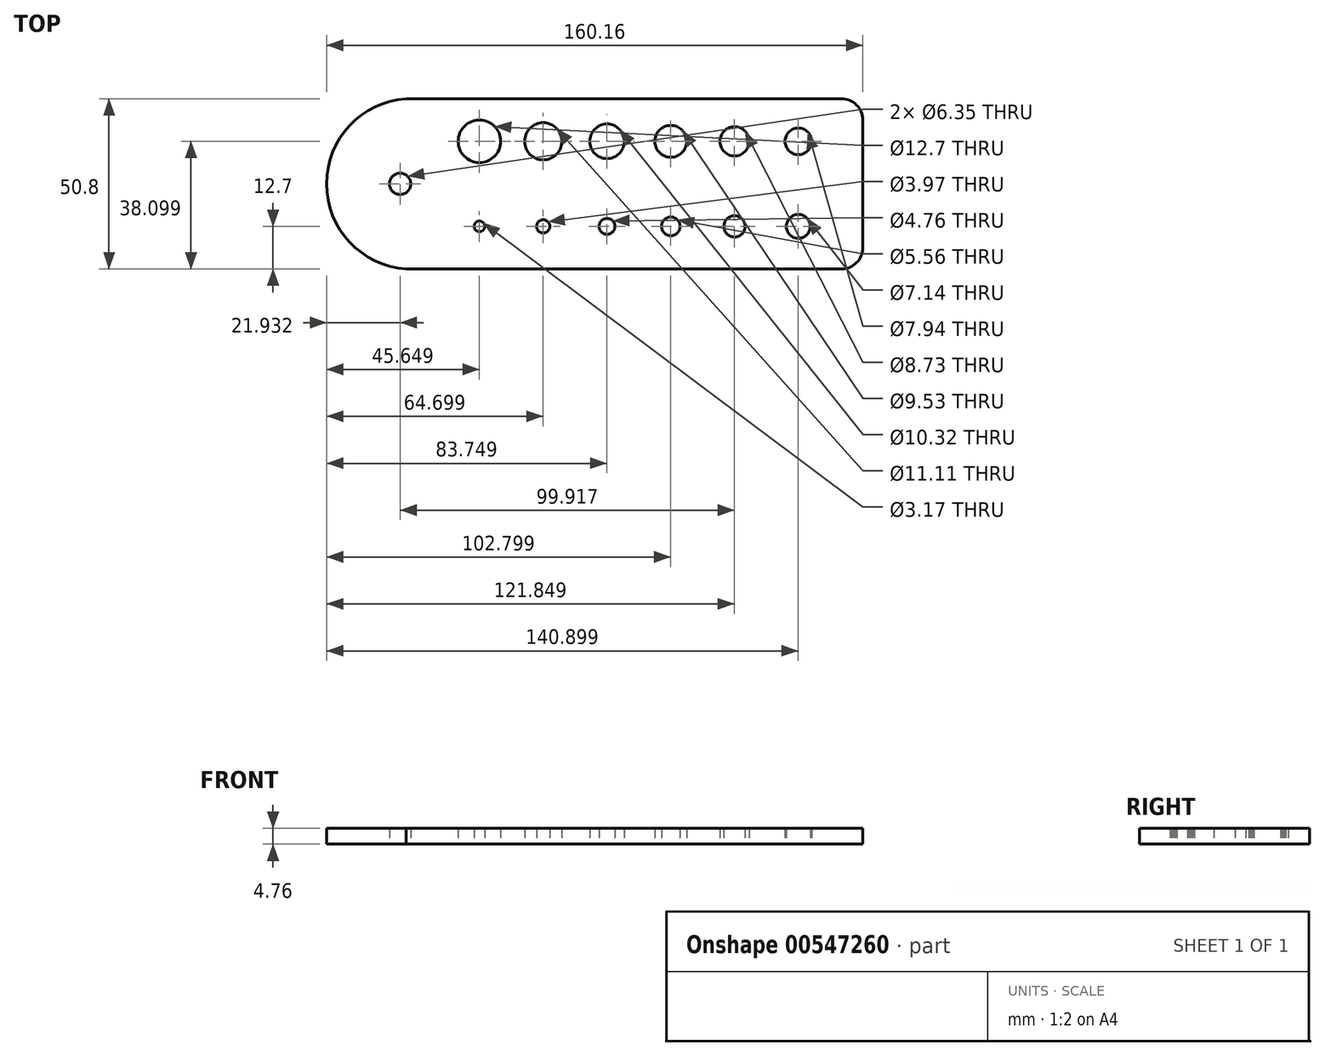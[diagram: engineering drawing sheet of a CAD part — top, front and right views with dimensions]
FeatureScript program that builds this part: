
annotation { "Feature Type Name" : "Feature", "Feature Type Description" : "" }
export const myFeature = defineFeature(function(context is Context, id is Id, definition is map)
    precondition{}
    {
        {
            var Q0;
            Q0=qCreatedBy(makeId("Top.planeOp"),FACE);
            var sketch = newSketch(context, id + "F0", { "sketchPlane" : qUnion([Q0])});
            skLineSegment(sketch, "E0.bottom", {"start": v(-46.8, 40.45) * mm, "end": v(83.22, 40.45) * mm});
            skLineSegment(sketch, "E0.top", {"start": v(-46.8, -10.35) * mm, "end": v(83.22, -10.35) * mm});
            skLineSegment(sketch, "E0.left", {"start": v(-62.83, 33.35) * mm, "end": v(-62.83, 33.35) * mm});
            skLineSegment(sketch, "E0.right", {"start": v(89.57, 34.1) * mm, "end": v(89.57, -4) * mm});
            skArc(sketch, "E1", {"start": v(-46.8, 40.45) * mm, "mid": v(-70.59, 15.05) * mm, "end": v(-46.8, -10.35) * mm});
            skPoint(sketch, "E2.visualSharp", {"position": v(89.57, -10.35) * mm});
            skArc(sketch, "E2.filletArc", {"start": v(83.22, -10.35) * mm, "mid": v(87.71, -8.5) * mm, "end": v(89.57, -4) * mm});
            skPoint(sketch, "E3.visualSharp", {"position": v(89.57, 40.45) * mm});
            skArc(sketch, "E3.filletArc", {"start": v(89.57, 34.1) * mm, "mid": v(87.71, 38.59) * mm, "end": v(83.22, 40.45) * mm});
            skSolve(sketch);
        }
        {
            var Q0;
            {var subQ5=sQuery(id+"F0.wireOp",EDGE,"E0.bottom");Q0=makeQuery(id+"F0.imprint","IMPRINT",FACE,{"disambiguationData":[TD([[makeQuery(id+"F0.imprint","IMPRINT",EDGE,{"derivedFrom":subQ5}),-1.0]])]});}
            var sketch = newSketch(context, id + "F1", { "sketchPlane" : qUnion([Q0])});
            skCircle(sketch, "E4", {"center": v(-24.94, 27.75) * mm, "radius": 6.35 * mm});
            skCircle(sketch, "E5", {"center": v(-5.9, 27.75) * mm, "radius": 5.56 * mm});
            skCircle(sketch, "E6", {"center": v(32.2, 27.75) * mm, "radius": 4.76 * mm});
            skCircle(sketch, "E7", {"center": v(51.26, 27.75) * mm, "radius": 4.37 * mm});
            skCircle(sketch, "E8", {"center": v(70.3, 27.75) * mm, "radius": 3.97 * mm});
            skCircle(sketch, "E9", {"center": v(13.16, 27.75) * mm, "radius": 5.16 * mm});
            skCircle(sketch, "E10", {"center": v(51.26, 2.35) * mm, "radius": 3.18 * mm});
            skCircle(sketch, "E11", {"center": v(32.2, 2.35) * mm, "radius": 2.78 * mm});
            skCircle(sketch, "E12", {"center": v(13.16, 2.35) * mm, "radius": 2.38 * mm});
            skCircle(sketch, "E13", {"center": v(70.3, 2.35) * mm, "radius": 3.57 * mm});
            skCircle(sketch, "E14", {"center": v(-5.9, 2.35) * mm, "radius": 1.98 * mm});
            skCircle(sketch, "E15", {"center": v(-24.94, 2.35) * mm, "radius": 1.59 * mm});
            skCircle(sketch, "E16", {"center": v(-48.66, 15.05) * mm, "radius": 3.18 * mm});
            skSolve(sketch);
        }
        {
            var Q0;
            Q0 = qSketchRegion(id + "F0", true);
            extrude(context, id + "F2", {"entities" : qUnion([Q0]), "depth" : 4.76 * mm, "offsetDistance" : 25.4 * mm});
        }
        {
            var Q0;
            Q0=makeQuery(id+"F1.imprint","IMPRINT",FACE,{"disambiguationData":[TD([[makeQuery(id+"F1.imprint","IMPRINT",EDGE,{"derivedFrom":sQuery(id+"F1.wireOp",EDGE,"E4")}),1.0]])]});
            var Q1;
            Q1=makeQuery(id+"F1.imprint","IMPRINT",FACE,{"disambiguationData":[TD([[makeQuery(id+"F1.imprint","IMPRINT",EDGE,{"derivedFrom":sQuery(id+"F1.wireOp",EDGE,"E15")}),1.0]])]});
            var Q2;
            Q2=makeQuery(id+"F1.imprint","IMPRINT",FACE,{"disambiguationData":[TD([[makeQuery(id+"F1.imprint","IMPRINT",EDGE,{"derivedFrom":sQuery(id+"F1.wireOp",EDGE,"E16")}),1.0]])]});
            var Q3;
            Q3=makeQuery(id+"F1.imprint","IMPRINT",FACE,{"disambiguationData":[TD([[makeQuery(id+"F1.imprint","IMPRINT",EDGE,{"derivedFrom":sQuery(id+"F1.wireOp",EDGE,"E5")}),1.0]])]});
            var Q4;
            Q4=makeQuery(id+"F1.imprint","IMPRINT",FACE,{"disambiguationData":[TD([[makeQuery(id+"F1.imprint","IMPRINT",EDGE,{"derivedFrom":sQuery(id+"F1.wireOp",EDGE,"E9")}),1.0]])]});
            var Q5;
            Q5=makeQuery(id+"F1.imprint","IMPRINT",FACE,{"disambiguationData":[TD([[makeQuery(id+"F1.imprint","IMPRINT",EDGE,{"derivedFrom":sQuery(id+"F1.wireOp",EDGE,"E6")}),1.0]])]});
            var Q6;
            Q6=makeQuery(id+"F1.imprint","IMPRINT",FACE,{"disambiguationData":[TD([[makeQuery(id+"F1.imprint","IMPRINT",EDGE,{"derivedFrom":sQuery(id+"F1.wireOp",EDGE,"E7")}),1.0]])]});
            var Q7;
            Q7=makeQuery(id+"F1.imprint","IMPRINT",FACE,{"disambiguationData":[TD([[makeQuery(id+"F1.imprint","IMPRINT",EDGE,{"derivedFrom":sQuery(id+"F1.wireOp",EDGE,"E8")}),1.0]])]});
            var Q8;
            Q8=makeQuery(id+"F1.imprint","IMPRINT",FACE,{"disambiguationData":[TD([[makeQuery(id+"F1.imprint","IMPRINT",EDGE,{"derivedFrom":sQuery(id+"F1.wireOp",EDGE,"E13")}),1.0]])]});
            var Q9;
            Q9=makeQuery(id+"F1.imprint","IMPRINT",FACE,{"disambiguationData":[TD([[makeQuery(id+"F1.imprint","IMPRINT",EDGE,{"derivedFrom":sQuery(id+"F1.wireOp",EDGE,"E10")}),1.0]])]});
            var Q10;
            Q10=makeQuery(id+"F1.imprint","IMPRINT",FACE,{"disambiguationData":[TD([[makeQuery(id+"F1.imprint","IMPRINT",EDGE,{"derivedFrom":sQuery(id+"F1.wireOp",EDGE,"E11")}),1.0]])]});
            var Q11;
            Q11=makeQuery(id+"F1.imprint","IMPRINT",FACE,{"disambiguationData":[TD([[makeQuery(id+"F1.imprint","IMPRINT",EDGE,{"derivedFrom":sQuery(id+"F1.wireOp",EDGE,"E12")}),1.0]])]});
            var Q12;
            Q12=makeQuery(id+"F1.imprint","IMPRINT",FACE,{"disambiguationData":[TD([[makeQuery(id+"F1.imprint","IMPRINT",EDGE,{"derivedFrom":sQuery(id+"F1.wireOp",EDGE,"E14")}),1.0]])]});
            extrude(context, id + "F3", {"entities" : qUnion([Q0, Q1, Q2, Q3, Q4, Q5, Q6, Q7, Q8, Q9, Q10, Q11, Q12]), "operationType" : NewBodyOperationType.REMOVE, "depth" : 35.56 * mm, "offsetDistance" : 25.4 * mm});
        }
    });
